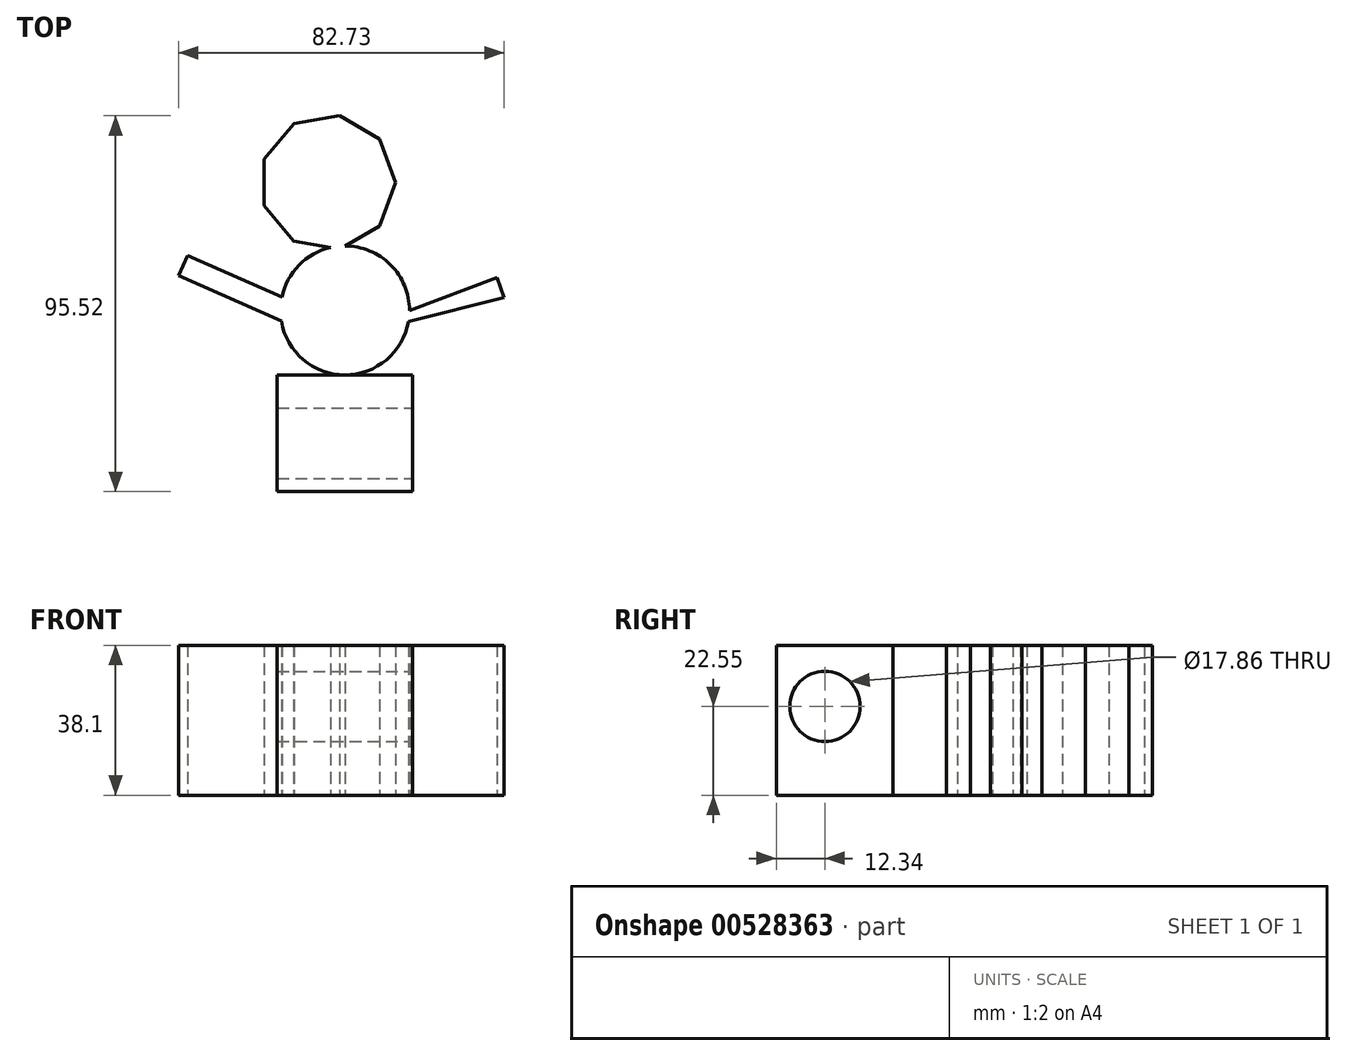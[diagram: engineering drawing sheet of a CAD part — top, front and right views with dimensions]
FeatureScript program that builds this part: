
annotation { "Feature Type Name" : "Feature", "Feature Type Description" : "" }
export const myFeature = defineFeature(function(context is Context, id is Id, definition is map)
    precondition{}
    {
        {
            var Q0;
            Q0=qCreatedBy(makeId("Top.planeOp"),FACE);
            var sketch = newSketch(context, id + "F0", { "sketchPlane" : qUnion([Q0])});
            skLineSegment(sketch, "E0.bottom", {"start": v(-20.9, 17.33) * mm, "end": v(13.53, 17.33) * mm});
            skLineSegment(sketch, "E0.top", {"start": v(-20.9, -12.34) * mm, "end": v(13.53, -12.34) * mm});
            skLineSegment(sketch, "E0.left", {"start": v(-20.9, 17.33) * mm, "end": v(-20.9, -12.34) * mm});
            skLineSegment(sketch, "E0.right", {"start": v(13.53, 17.33) * mm, "end": v(13.53, -12.34) * mm});
            skCircle(sketch, "E1", {"center": v(-3.68, 33.71) * mm, "radius": 16.38 * mm});
            skPoint(sketch, "E1.centerSnap0", {"position": v(-3.68, 17.33) * mm});
            skLineSegment(sketch, "E2", {"start": v(12.7, 33.7) * mm, "end": v(34.9, 42.02) * mm});
            skLineSegment(sketch, "E3", {"start": v(-19.71, 37.1) * mm, "end": v(-43.68, 47.72) * mm});
            skLineSegment(sketch, "E4", {"start": v(-43.68, 47.72) * mm, "end": v(-45.96, 42.59) * mm});
            skLineSegment(sketch, "E5", {"start": v(-45.96, 42.59) * mm, "end": v(-19.84, 31) * mm});
            skLineSegment(sketch, "E6", {"start": v(34.9, 42.02) * mm, "end": v(36.77, 37.03) * mm});
            skLineSegment(sketch, "E7", {"start": v(36.77, 37.03) * mm, "end": v(12.45, 30.9) * mm});
            skCircle(sketch, "E8.cCircle", {"center": v(-8.07, 66.24) * mm, "radius": 16.17 * mm, "construction": true});
            skLineSegment(sketch, "E8.0", {"start": v(5.1, 55.17) * mm, "end": v(-5.1, 49.3) * mm});
            skLineSegment(sketch, "E8.1", {"start": v(-5.1, 49.3) * mm, "end": v(-16.69, 51.35) * mm});
            skLineSegment(sketch, "E8.2", {"start": v(-16.69, 51.35) * mm, "end": v(-24.24, 60.37) * mm});
            skLineSegment(sketch, "E8.3", {"start": v(-24.24, 60.37) * mm, "end": v(-24.23, 72.14) * mm});
            skLineSegment(sketch, "E8.4", {"start": v(-24.23, 72.14) * mm, "end": v(-16.66, 81.15) * mm});
            skLineSegment(sketch, "E8.5", {"start": v(-16.66, 81.15) * mm, "end": v(-5.07, 83.18) * mm});
            skLineSegment(sketch, "E8.6", {"start": v(-5.07, 83.18) * mm, "end": v(5.12, 77.29) * mm});
            skLineSegment(sketch, "E8.7", {"start": v(5.12, 77.29) * mm, "end": v(9.13, 66.23) * mm});
            skLineSegment(sketch, "E8.8", {"start": v(9.13, 66.23) * mm, "end": v(5.1, 55.17) * mm});
            skPoint(sketch, "E8.0.midPoint", {"position": v(0, 52.23) * mm});
            skSolve(sketch);
        }
        {
            var Q0;
            Q0 = qSketchRegion(id + "F0", true);
            extrude(context, id + "F1", {"entities" : qUnion([Q0]), "depth" : 38.1 * mm, "offsetDistance" : 25.4 * mm});
        }
        {
            var Q0;
            Q0=makeQuery(id+"F1.opExtrude","SWEPT_FACE",FACE,{"disambiguationData":[OSD([sQuery(id+"F0.wireOp",EDGE,"E0.right")])]});
            var sketch = newSketch(context, id + "F2", { "sketchPlane" : qUnion([Q0])});
            skCircle(sketch, "E9", {"center": v(0, 22.55) * mm, "radius": 8.93 * mm});
            skSolve(sketch);
        }
        {
            var Q0;
            Q0 = qSketchRegion(id + "F2", true);
            extrude(context, id + "F3", {"entities" : qUnion([Q0]), "operationType" : NewBodyOperationType.REMOVE, "oppositeDirection" : true, "depth" : 76.2 * mm, "offsetDistance" : 25.4 * mm});
        }
    });
